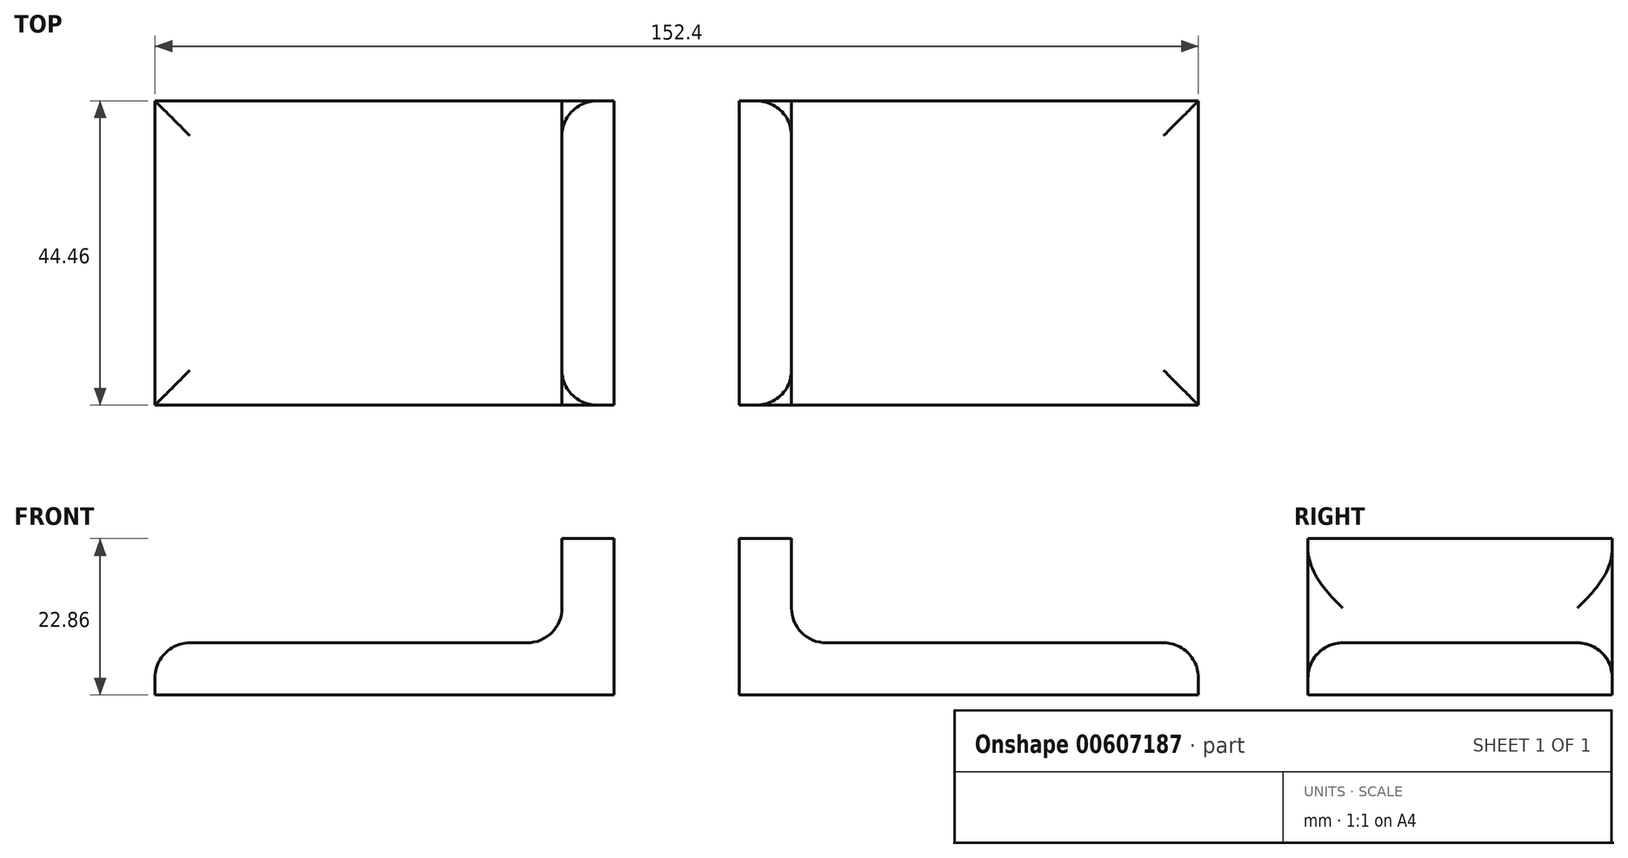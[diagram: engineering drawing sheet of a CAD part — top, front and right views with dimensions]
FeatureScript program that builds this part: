
annotation { "Feature Type Name" : "Feature", "Feature Type Description" : "" }
export const myFeature = defineFeature(function(context is Context, id is Id, definition is map)
    precondition{}
    {
        {
            var Q0;
            Q0=qCreatedBy(makeId("Top.planeOp"),FACE);
            var sketch = newSketch(context, id + "F0", { "sketchPlane" : qUnion([Q0])});
            skLineSegment(sketch, "E0.bottom", {"start": v(-76.2, 22.23) * mm, "end": v(76.2, 22.23) * mm});
            skLineSegment(sketch, "E0.top", {"start": v(-76.2, -22.23) * mm, "end": v(76.2, -22.23) * mm});
            skLineSegment(sketch, "E0.left", {"start": v(-76.2, 22.23) * mm, "end": v(-76.2, -22.23) * mm});
            skLineSegment(sketch, "E0.right", {"start": v(76.2, 22.23) * mm, "end": v(76.2, -22.23) * mm});
            skPoint(sketch, "E0.middle", {"position": v(0, 0) * mm});
            skLineSegment(sketch, "E1.bottom", {"start": v(-16.76, 22.23) * mm, "end": v(16.76, 22.23) * mm});
            skLineSegment(sketch, "E1.top", {"start": v(-16.76, -22.23) * mm, "end": v(16.76, -22.23) * mm});
            skLineSegment(sketch, "E1.left", {"start": v(-16.76, 22.23) * mm, "end": v(-16.76, -22.23) * mm});
            skLineSegment(sketch, "E1.right", {"start": v(16.76, 22.23) * mm, "end": v(16.76, -22.23) * mm});
            skLineSegment(sketch, "E2.bottom", {"start": v(-9.14, 22.23) * mm, "end": v(9.14, 22.23) * mm});
            skLineSegment(sketch, "E2.top", {"start": v(-9.14, -22.23) * mm, "end": v(9.14, -22.23) * mm});
            skLineSegment(sketch, "E2.left", {"start": v(-9.14, 22.23) * mm, "end": v(-9.14, -22.23) * mm});
            skLineSegment(sketch, "E2.right", {"start": v(9.14, 22.23) * mm, "end": v(9.14, -22.23) * mm});
            skSolve(sketch);
        }
        {
            var Q0;
            {var subQ0=sQuery(id+"F0.wireOp",EDGE,"E0.left");Q0=makeQuery(id+"F0.imprint","IMPRINT",FACE,{"disambiguationData":[TD([[makeQuery(id+"F0.imprint","IMPRINT",EDGE,{"derivedFrom":subQ0}),1.0]])]});}
            var Q1;
            {var subQ0=sQuery(id+"F0.wireOp",EDGE,"E1.left");Q1=makeQuery(id+"F0.imprint","IMPRINT",FACE,{"disambiguationData":[TD([[makeQuery(id+"F0.imprint","IMPRINT",EDGE,{"derivedFrom":subQ0}),1.0]])]});}
            var Q2;
            Q2=makeQuery(id+"F0.imprint","IMPRINT",FACE,{"disambiguationData":[TD([[makeQuery(id+"F0.imprint","IMPRINT",EDGE,{"derivedFrom":sQuery(id+"F0.wireOp",EDGE,"E2.bottom")}),-1.0]])]});
            var Q3;
            {var subQ0=sQuery(id+"F0.wireOp",EDGE,"E1.right");Q3=makeQuery(id+"F0.imprint","IMPRINT",FACE,{"disambiguationData":[TD([[makeQuery(id+"F0.imprint","IMPRINT",EDGE,{"derivedFrom":subQ0}),-1.0]])]});}
            var Q4;
            {var subQ0=sQuery(id+"F0.wireOp",EDGE,"E0.right");Q4=makeQuery(id+"F0.imprint","IMPRINT",FACE,{"disambiguationData":[TD([[makeQuery(id+"F0.imprint","IMPRINT",EDGE,{"derivedFrom":subQ0}),-1.0]])]});}
            extrude(context, id + "F1", {"entities" : qUnion([Q0, Q1, Q2, Q3, Q4]), "oppositeDirection" : true, "depth" : 7.62 * mm, "offsetDistance" : 25.4 * mm});
        }
        {
            var Q0;
            {var subQ0=sQuery(id+"F0.wireOp",EDGE,"E1.left");Q0=makeQuery(id+"F0.imprint","IMPRINT",FACE,{"disambiguationData":[TD([[makeQuery(id+"F0.imprint","IMPRINT",EDGE,{"derivedFrom":subQ0}),1.0]])]});}
            var Q1;
            {var subQ0=sQuery(id+"F0.wireOp",EDGE,"E1.right");Q1=makeQuery(id+"F0.imprint","IMPRINT",FACE,{"disambiguationData":[TD([[makeQuery(id+"F0.imprint","IMPRINT",EDGE,{"derivedFrom":subQ0}),-1.0]])]});}
            extrude(context, id + "F2", {"entities" : qUnion([Q0, Q1]), "operationType" : NewBodyOperationType.ADD, "depth" : 15.24 * mm, "offsetDistance" : 25.4 * mm});
        }
        {
            var Q0;
            {var subQ1=sQuery(id+"F0.wireOp",EDGE,"E1.bottom");var subQ2=sQuery(id+"F0.wireOp",EDGE,"E0.bottom");var subQ4=sQuery(id+"F0.wireOp",EDGE,"E2.bottom");var subQ5=sQuery(id+"F0.wireOp",EDGE,"E0.right");var subQ6=sQuery(id+"F0.wireOp",EDGE,"E2.top");var subQ7=sQuery(id+"F0.wireOp",EDGE,"E1.top");var subQ8=sQuery(id+"F0.wireOp",EDGE,"E0.top");Q0=makeQuery(id+"F2.boolean.opBoolean","SPLIT",FACE,{"disambiguationData":[TD([makeQuery(id+"F1.opExtrude","SWEPT_FACE",FACE,{"disambiguationData":[OSD([subQ5])]})])],"derivedFrom":makeQuery(id+"F1.opExtrude","CAP_FACE",FACE,{"disambiguationData":[OSD([subQ2,subQ8,sQuery(id+"F0.wireOp",EDGE,"E0.left"),subQ5,subQ1,subQ7,subQ4,subQ6])],"isStart":true})});}
            var Q1;
            {var subQ1=sQuery(id+"F0.wireOp",EDGE,"E1.bottom");var subQ2=sQuery(id+"F0.wireOp",EDGE,"E0.bottom");var subQ4=sQuery(id+"F0.wireOp",EDGE,"E2.bottom");var subQ5=sQuery(id+"F0.wireOp",EDGE,"E0.left");var subQ6=sQuery(id+"F0.wireOp",EDGE,"E2.top");var subQ7=sQuery(id+"F0.wireOp",EDGE,"E1.top");var subQ8=sQuery(id+"F0.wireOp",EDGE,"E0.top");Q1=makeQuery(id+"F2.boolean.opBoolean","SPLIT",FACE,{"disambiguationData":[TD([makeQuery(id+"F1.opExtrude","SWEPT_FACE",FACE,{"disambiguationData":[OSD([subQ5])]})])],"derivedFrom":makeQuery(id+"F1.opExtrude","CAP_FACE",FACE,{"disambiguationData":[OSD([subQ2,subQ8,subQ5,sQuery(id+"F0.wireOp",EDGE,"E0.right"),subQ1,subQ7,subQ4,subQ6])],"isStart":true})});}
            fillet(context, id + "F3", {"entities" : qUnion([Q0, Q1]), "radius" : 5.08 * mm, "tangentPropagation" : true, "allowEdgeOverflow" : false});
        }
    });
